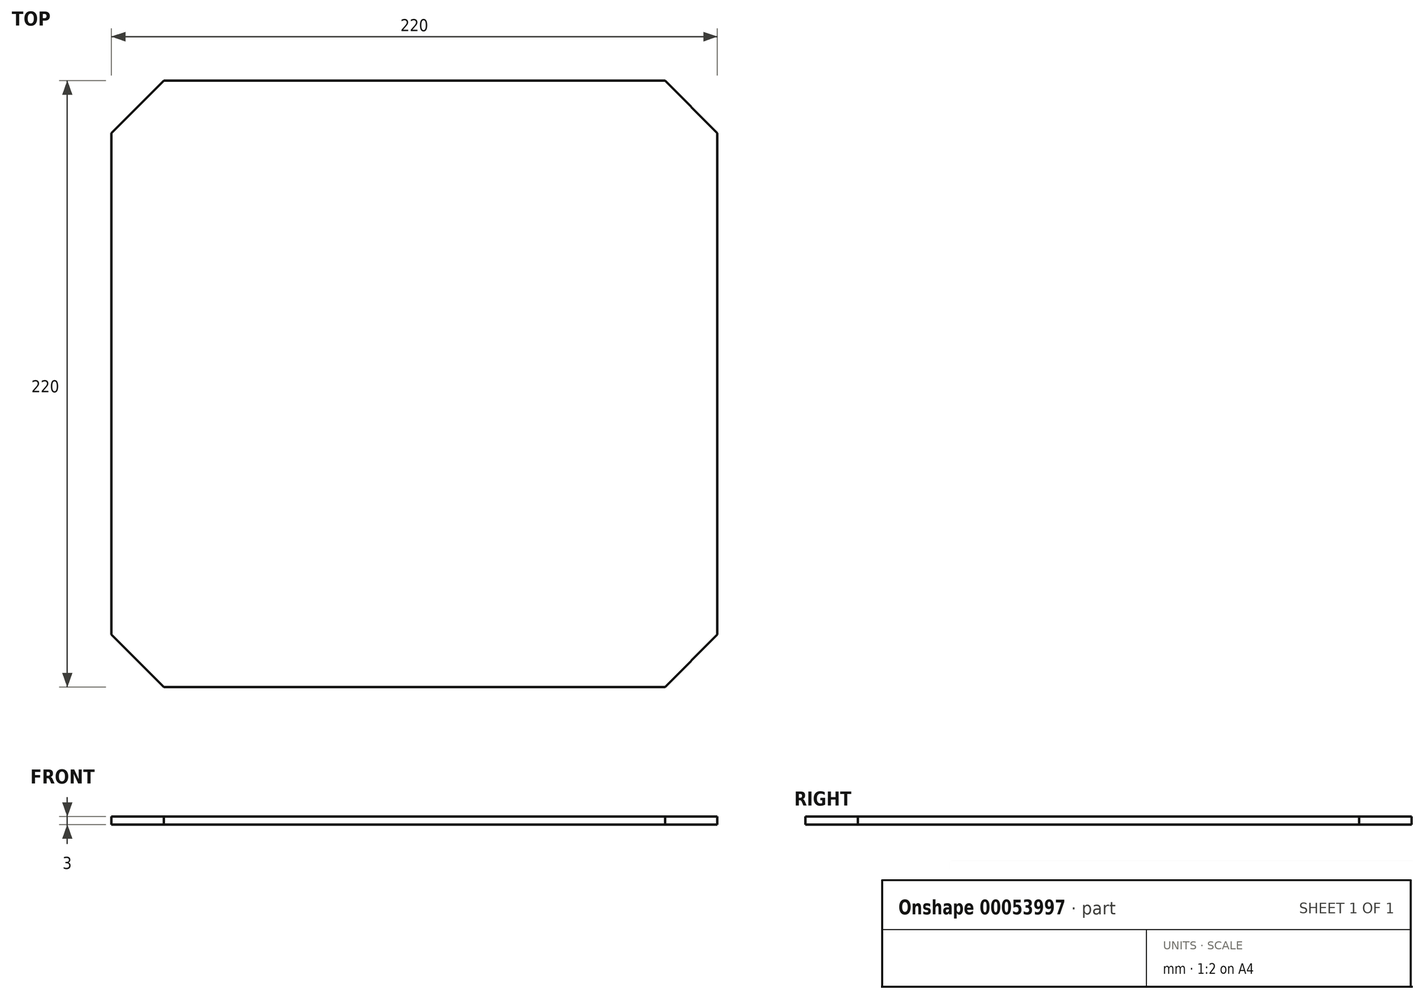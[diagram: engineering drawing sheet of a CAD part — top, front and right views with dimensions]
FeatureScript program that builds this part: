
annotation { "Feature Type Name" : "Feature", "Feature Type Description" : "" }
export const myFeature = defineFeature(function(context is Context, id is Id, definition is map)
    precondition{}
    {
        {
            var Q0;
            Q0=qCreatedBy(makeId("Top.planeOp"),FACE);
            var sketch = newSketch(context, id + "F0", { "sketchPlane" : qUnion([Q0])});
            skLineSegment(sketch, "E0.rect.bottom", {"start": v(110, -110) * mm, "end": v(-110, -110) * mm});
            skLineSegment(sketch, "E0.rect.top", {"start": v(110, 110) * mm, "end": v(-110, 110) * mm});
            skLineSegment(sketch, "E0.rect.left", {"start": v(110, -110) * mm, "end": v(110, 110) * mm});
            skLineSegment(sketch, "E0.rect.right", {"start": v(-110, -110) * mm, "end": v(-110, 110) * mm});
            skPoint(sketch, "E0.rect.middle", {"position": v(0, 0) * mm});
            skSolve(sketch);
        }
        {
            var Q0;
            Q0=qSketchRegion(id+"F0",true);
            extrude(context, id + "F1", {"entities" : qUnion([Q0]), "depth" : 3 * mm});
        }
        {
            var Q0;
            Q0=makeQuery(id+"F1.opExtrude","SWEPT_EDGE",EDGE,{"disambiguationData":[OSD([sQuery(id+"F0.wireOp",EDGE,"E0.rect.bottom"),sQuery(id+"F0.wireOp",EDGE,"E0.rect.right")])]});
            var Q1;
            Q1=makeQuery(id+"F1.opExtrude","SWEPT_EDGE",EDGE,{"disambiguationData":[OSD([sQuery(id+"F0.wireOp",EDGE,"E0.rect.bottom"),sQuery(id+"F0.wireOp",EDGE,"E0.rect.left")])]});
            var Q2;
            Q2=makeQuery(id+"F1.opExtrude","SWEPT_EDGE",EDGE,{"disambiguationData":[OSD([sQuery(id+"F0.wireOp",EDGE,"E0.rect.top"),sQuery(id+"F0.wireOp",EDGE,"E0.rect.right")])]});
            var Q3;
            Q3=makeQuery(id+"F1.opExtrude","SWEPT_EDGE",EDGE,{"disambiguationData":[OSD([sQuery(id+"F0.wireOp",EDGE,"E0.rect.top"),sQuery(id+"F0.wireOp",EDGE,"E0.rect.left")])]});
            chamfer(context, id + "F2", {"entities" : qUnion([Q0, Q1, Q2, Q3]), "width" : 19 * mm, "tangentPropagation" : true});
        }
    });
